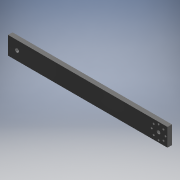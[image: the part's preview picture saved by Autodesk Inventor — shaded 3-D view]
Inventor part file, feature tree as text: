
AUTODESK INVENTOR PART (.ipt)
format: ipt  version: 2019 (Build 230136000, 136)  size: 133,120 bytes
history: native  units: mm (DEFAULTED — no unit token found)
features: extrude x4, sketch x4
ambient origin geometry x8: Origin, YZ Plane, XZ Plane, XY Plane, X Axis, Y Axis, Z Axis, Center Point
bodies: Solid1 (feature_tree)
feature tree (8):
  extrude  "Extrusion1"  Depth=25.4mm
  extrude  "Extrusion2"  Depth=6.35mm
  extrude  "Extrusion3"  Depth=25.4mm
  extrude  "Extrusion4"  Depth=25.4mm
  sketch  "Sketch1"  dims[d0=225.806mm d1=25.4mm]
  sketch  "Sketch2"  dims[d2=6.35mm d3=0.0mm d4=12.7mm]
  sketch  "Sketch3"  dims[d5=25.4mm d6=5.7658mm]
  sketch  "Sketch4"  dims[d7=2.5mm d8=0.0mm d9=25.4mm d10=12.7mm d11=12.7mm d12=5.08mm d13=10.0mm d14=0.0mm d15=12.7mm d16=19.558mm d17=7.493mm d18=2.7178mm d19=2.7178mm d20=2.7178mm d21=2.7178mm d22=2.7178mm d23=2.7178mm d24=2.7178mm d25=2.7178mm d26=25.4mm d27=0.0mm]
